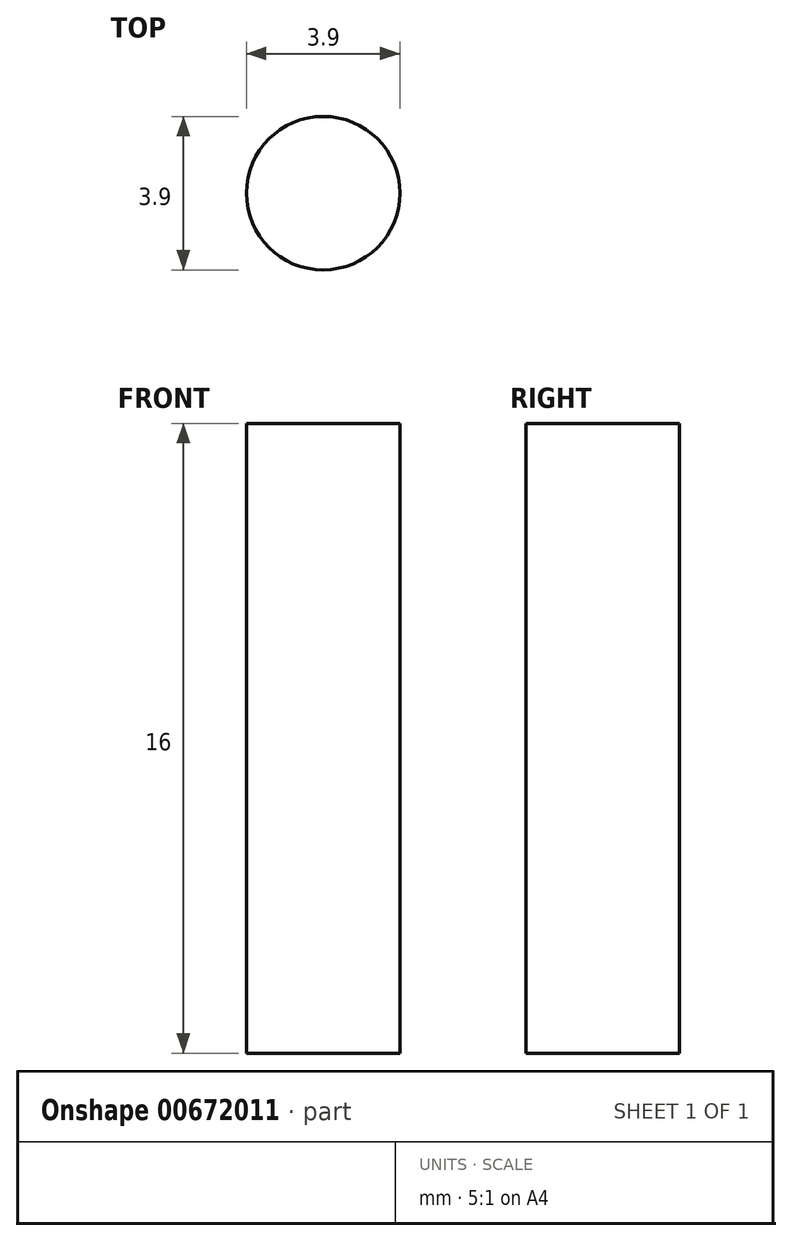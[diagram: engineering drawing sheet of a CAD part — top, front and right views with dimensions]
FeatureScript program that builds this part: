
annotation { "Feature Type Name" : "Feature", "Feature Type Description" : "" }
export const myFeature = defineFeature(function(context is Context, id is Id, definition is map)
    precondition{}
    {
        {
            var Q0;
            Q0=qCreatedBy(makeId("Top.planeOp"),FACE);
            var sketch = newSketch(context, id + "F0", { "sketchPlane" : qUnion([Q0])});
            skCircle(sketch, "E0", {"center": v(0, 0) * mm, "radius": 1.95 * mm});
            skSolve(sketch);
        }
        {
            var Q0;
            Q0=makeQuery(id+"F0.imprint","IMPRINT",FACE,{"disambiguationData":[TD([[makeQuery(id+"F0.imprint","IMPRINT",EDGE,{"derivedFrom":sQuery(id+"F0.wireOp",EDGE,"E0")}),1.0]])]});
            extrude(context, id + "F1", {"entities" : qUnion([Q0]), "depth" : 16 * mm, "offsetDistance" : 25 * mm});
        }
    });
